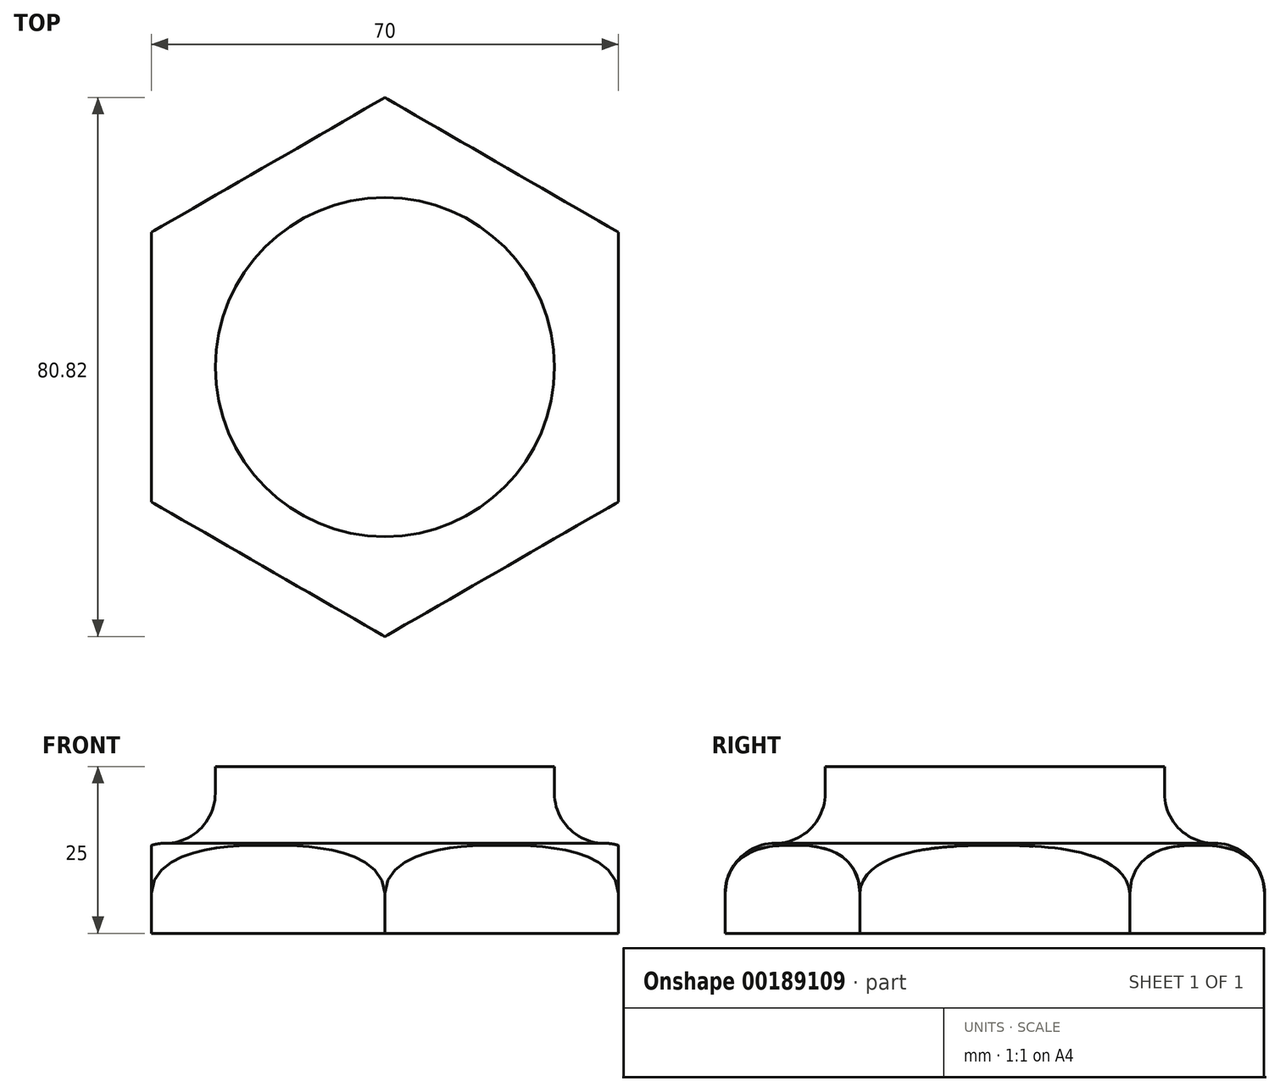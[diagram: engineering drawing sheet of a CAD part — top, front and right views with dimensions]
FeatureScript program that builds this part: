
annotation { "Feature Type Name" : "Feature", "Feature Type Description" : "" }
export const myFeature = defineFeature(function(context is Context, id is Id, definition is map)
    precondition{}
    {
        {
            var Q0;
            Q0=qCreatedBy(makeId("Top.planeOp"),FACE);
            var sketch = newSketch(context, id + "F0", { "sketchPlane" : qUnion([Q0])});
            skCircle(sketch, "E0.cCircle", {"center": v(0, 0) * mm, "radius": 35 * mm, "construction": true});
            skLineSegment(sketch, "E0.0", {"start": v(-35, -20.2) * mm, "end": v(-35, 20.2) * mm});
            skLineSegment(sketch, "E0.1", {"start": v(-35, 20.2) * mm, "end": v(0, 40.41) * mm});
            skLineSegment(sketch, "E0.2", {"start": v(0, 40.41) * mm, "end": v(35, 20.2) * mm});
            skLineSegment(sketch, "E0.3", {"start": v(35, 20.2) * mm, "end": v(35, -20.2) * mm});
            skLineSegment(sketch, "E0.4", {"start": v(35, -20.2) * mm, "end": v(0, -40.41) * mm});
            skLineSegment(sketch, "E0.5", {"start": v(0, -40.41) * mm, "end": v(-35, -20.2) * mm});
            skPoint(sketch, "E0.0.midPoint", {"position": v(-35, 0) * mm});
            skSolve(sketch);
        }
        {
            var Q0;
            Q0=makeQuery(id+"F0.imprint","IMPRINT",FACE,{"disambiguationData":[TD([[makeQuery(id+"F0.imprint","IMPRINT",EDGE,{"derivedFrom":sQuery(id+"F0.wireOp",EDGE,"E0.0")}),-1.0]])]});
            extrude(context, id + "F1", {"entities" : qUnion([Q0]), "depth" : 25 * mm});
        }
        {
            var Q0;
            Q0=qCreatedBy(makeId("Right.planeOp"),FACE);
            var sketch = newSketch(context, id + "F2", { "sketchPlane" : qUnion([Q0])});
            skLineSegment(sketch, "E1.0.0", {"start": v(40.41, 0) * mm, "end": v(20.2, 0) * mm});
            skLineSegment(sketch, "E1.0.1", {"start": v(20.2, 0) * mm, "end": v(20.2, 25) * mm});
            skLineSegment(sketch, "E1.0.2", {"start": v(20.2, 25) * mm, "end": v(40.41, 25) * mm});
            skLineSegment(sketch, "E1.0.3", {"start": v(40.41, 25) * mm, "end": v(40.41, 0) * mm});
            skLineSegment(sketch, "E2.0.0", {"start": v(20.2, 0) * mm, "end": v(-20.2, 0) * mm});
            skLineSegment(sketch, "E2.0.1", {"start": v(-20.2, 0) * mm, "end": v(-20.2, 25) * mm});
            skLineSegment(sketch, "E2.0.2", {"start": v(-20.2, 25) * mm, "end": v(20.2, 25) * mm});
            skLineSegment(sketch, "E2.0.3", {"start": v(20.2, 25) * mm, "end": v(20.2, 0) * mm});
            skLineSegment(sketch, "E3.0.0", {"start": v(-20.2, 0) * mm, "end": v(-40.41, 0) * mm});
            skLineSegment(sketch, "E3.0.1", {"start": v(-40.41, 0) * mm, "end": v(-40.41, 25) * mm});
            skLineSegment(sketch, "E3.0.2", {"start": v(-40.41, 25) * mm, "end": v(-20.2, 25) * mm});
            skLineSegment(sketch, "E3.0.3", {"start": v(-20.2, 25) * mm, "end": v(-20.2, 0) * mm});
            skLineSegment(sketch, "E4", {"start": v(40.41, 0) * mm, "end": v(40.41, 6) * mm});
            skLineSegment(sketch, "E5", {"start": v(40.41, 6) * mm, "end": v(32.91, 6) * mm});
            skLineSegment(sketch, "E6", {"start": v(32.91, 6) * mm, "end": v(32.91, 21) * mm});
            skArc(sketch, "E7", {"start": v(25.41, 21) * mm, "mid": v(27.61, 15.7) * mm, "end": v(32.91, 13.5) * mm});
            skLineSegment(sketch, "E8", {"start": v(25.41, 21) * mm, "end": v(25.41, 25) * mm});
            skArc(sketch, "E9.trimOffspring", {"start": v(40.41, 6) * mm, "mid": v(38.22, 11.3) * mm, "end": v(32.91, 13.5) * mm});
            skLineSegment(sketch, "E10", {"start": v(40.41, 6) * mm, "end": v(40.41, 25) * mm});
            skSolve(sketch);
        }
        {
            var Q0;
            Q0=qCreatedBy(makeId("Right.planeOp"),FACE);
            var sketch = newSketch(context, id + "F3", { "sketchPlane" : qUnion([Q0])});
            skLineSegment(sketch, "E11", {"start": v(0, 0) * mm, "end": v(0, 24.97) * mm});
            skSolve(sketch);
        }
        {
            var Q0;
            Q0=makeQuery(id+"F2.imprint","IMPRINT",FACE,{"disambiguationData":[TD([[makeQuery(id+"F2.imprint","IMPRINT",EDGE,{"derivedFrom":sQuery(id+"F2.wireOp",EDGE,"E7")}),1.0]])]});
            var Q1;
            Q1=sQuery(id+"F3.wireOp",EDGE,"E11");
            revolve(context, id + "F4", {"operationType" : NewBodyOperationType.REMOVE, "entities" : qUnion([Q0]), "axis" : qUnion([Q1]), "revolveType" : RevolveType.FULL, "oppositeDirection" : true});
        }
    });
